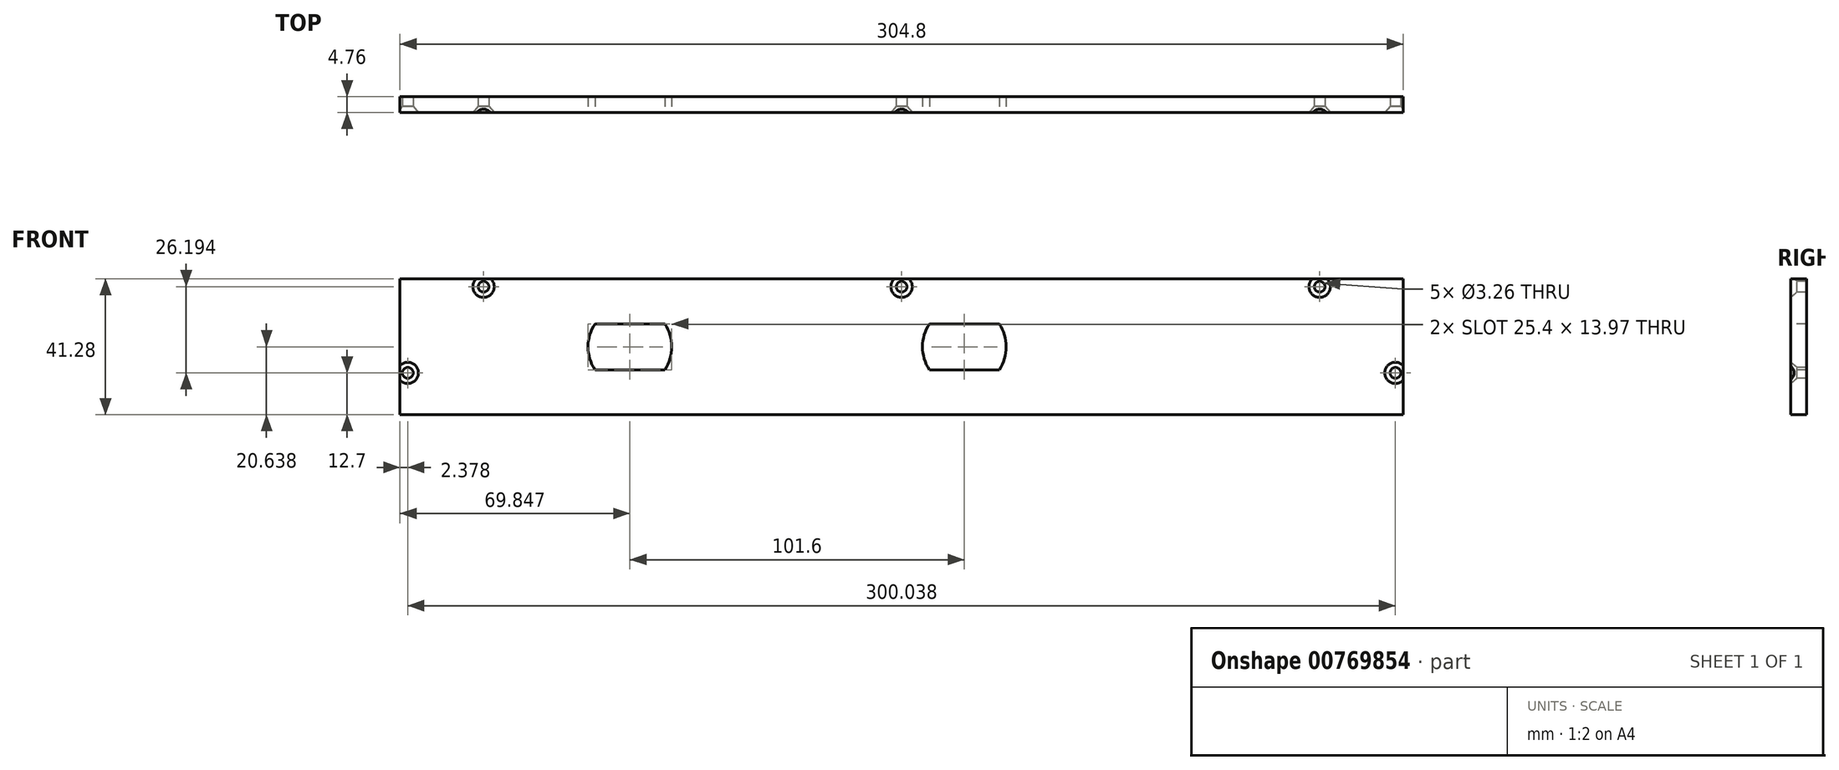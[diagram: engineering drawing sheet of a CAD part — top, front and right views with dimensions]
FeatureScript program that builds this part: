
annotation { "Feature Type Name" : "Feature", "Feature Type Description" : "" }
export const myFeature = defineFeature(function(context is Context, id is Id, definition is map)
    precondition{}
    {
        {
            var Q0;
            Q0=qCreatedBy(makeId("Front.planeOp"),FACE);
            var sketch = newSketch(context, id + "F0", { "sketchPlane" : qUnion([Q0])});
            skLineSegment(sketch, "E0.bottom", {"start": v(-119.12, 56.77) * mm, "end": v(185.68, 56.77) * mm});
            skLineSegment(sketch, "E0.top", {"start": v(-119.12, 15.5) * mm, "end": v(185.68, 15.5) * mm});
            skLineSegment(sketch, "E0.left", {"start": v(-119.12, 56.77) * mm, "end": v(-119.12, 15.5) * mm});
            skLineSegment(sketch, "E0.right", {"start": v(185.68, 56.77) * mm, "end": v(185.68, 15.5) * mm});
            skSolve(sketch);
        }
        {
            var Q0;
            Q0 = qSketchRegion(id + "F0", true);
            extrude(context, id + "F1", {"entities" : qUnion([Q0]), "depth" : 4.76 * mm, "offsetDistance" : 25.4 * mm});
        }
        {
            var Q0;
            Q0=makeQuery(id+"F1.opExtrude","CAP_FACE",FACE,{"disambiguationData":[OSD([sQuery(id+"F0.wireOp",EDGE,"E0.bottom"),sQuery(id+"F0.wireOp",EDGE,"E0.top"),sQuery(id+"F0.wireOp",EDGE,"E0.left"),sQuery(id+"F0.wireOp",EDGE,"E0.right")])],"isStart":false});
            var sketch = newSketch(context, id + "F2", { "sketchPlane" : qUnion([Q0])});
            skLineSegment(sketch, "E1", {"start": v(-116.74, 56.77) * mm, "end": v(-116.74, 15.5) * mm, "construction": true});
            skLineSegment(sketch, "E2", {"start": v(-119.12, 54.38) * mm, "end": v(185.68, 54.38) * mm, "construction": true});
            skLineSegment(sketch, "E3", {"start": v(183.3, 15.5) * mm, "end": v(183.3, 56.77) * mm, "construction": true});
            skPoint(sketch, "E4", {"position": v(-116.74, 28.2) * mm});
            skPoint(sketch, "E5", {"position": v(183.3, 28.2) * mm});
            skPoint(sketch, "E6", {"position": v(160.28, 54.38) * mm});
            skPoint(sketch, "E7", {"position": v(33.28, 54.38) * mm});
            skPoint(sketch, "E8", {"position": v(-93.72, 54.38) * mm});
            skSolve(sketch);
        }
        {
            var Q0;
            Q0=sQuery(id+"F2.wireOp",VERTEX,"E8");
            var Q1;
            Q1=sQuery(id+"F2.wireOp",VERTEX,"E4");
            var Q2;
            Q2=sQuery(id+"F2.wireOp",VERTEX,"E7");
            var Q3;
            Q3=sQuery(id+"F2.wireOp",VERTEX,"E6");
            var Q4;
            Q4=sQuery(id+"F2.wireOp",VERTEX,"E5");
            var Q5;
            Q5=makeQuery(id+"F1.opExtrude","SWEPT_BODY",BODY,{"disambiguationData":[OSD([sQuery(id+"F0.wireOp",EDGE,"E0.bottom"),sQuery(id+"F0.wireOp",EDGE,"E0.top"),sQuery(id+"F0.wireOp",EDGE,"E0.left"),sQuery(id+"F0.wireOp",EDGE,"E0.right")])]});
            hole(context, id + "F3", {"style" : HoleStyle.C_SINK, "endStyle" : HoleEndStyle.BLIND, "standardTappedOrClearance" : lookupTablePath({ "standard" : "ANSI", "fit" : "Normal (ASME)", "size" : "#4", "type" : "Clearance" }), "standardBlindInLast" : lookupTablePath({ "fit" : "Free", "standard" : "ANSI", "size" : "#4", "type" : "Clearance" }), "holeDiameter" : 3.26 * mm, "cSinkDiameter" : 6.48 * mm, "cSinkAngle" : 82 * degree, "majorDiameter" : 2.84 * mm, "holeDepth" : 14.6 * mm, "tappedDepth" : 12.7 * mm, "tapClearance" : 3, "locations" : qUnion([Q0, Q1, Q2, Q3, Q4]), "scope" : qUnion([Q5])});
        }
        {
            var Q0;
            Q0=makeQuery(id+"F1.opExtrude","CAP_FACE",FACE,{"disambiguationData":[OSD([sQuery(id+"F0.wireOp",EDGE,"E0.bottom"),sQuery(id+"F0.wireOp",EDGE,"E0.top"),sQuery(id+"F0.wireOp",EDGE,"E0.left"),sQuery(id+"F0.wireOp",EDGE,"E0.right")])],"isStart":false});
            var sketch = newSketch(context, id + "F4", { "sketchPlane" : qUnion([Q0])});
            skLineSegment(sketch, "E9", {"start": v(33.28, 15.5) * mm, "end": v(33.28, 56.77) * mm, "construction": true});
            skLineSegment(sketch, "E10", {"start": v(31.08, 56.77) * mm, "end": v(35.47, 56.77) * mm, "construction": true});
            skLineSegment(sketch, "E11", {"start": v(-119.12, 56.77) * mm, "end": v(-119.12, 15.5) * mm, "construction": true});
            skLineSegment(sketch, "E12", {"start": v(185.68, 56.77) * mm, "end": v(185.68, 15.5) * mm, "construction": true});
            skLineSegment(sketch, "E13", {"start": v(-119.12, 36.13) * mm, "end": v(185.68, 36.13) * mm, "construction": true});
            skArc(sketch, "E14", {"start": v(-59.88, 43.11) * mm, "mid": v(-61.97, 36.13) * mm, "end": v(-59.88, 29.14) * mm});
            skLineSegment(sketch, "E15.bottom", {"start": v(-59.88, 43.11) * mm, "end": v(-38.67, 43.11) * mm});
            skLineSegment(sketch, "E15.top", {"start": v(-59.88, 29.14) * mm, "end": v(-38.67, 29.14) * mm});
            skLineSegment(sketch, "E15.left", {"start": v(-59.88, 43.11) * mm, "end": v(-59.88, 29.14) * mm, "construction": true});
            skLineSegment(sketch, "E15.right", {"start": v(-38.67, 43.11) * mm, "end": v(-38.67, 29.14) * mm, "construction": true});
            skArc(sketch, "E16.trimOffspring", {"start": v(-38.67, 29.14) * mm, "mid": v(-36.57, 36.13) * mm, "end": v(-38.67, 43.11) * mm});
            skArc(sketch, "E17.MirrorCS", {"start": v(62.93, 43.11) * mm, "mid": v(65.03, 36.13) * mm, "end": v(62.93, 29.14) * mm});
            skLineSegment(sketch, "E18.MirrorCS", {"start": v(62.93, 43.11) * mm, "end": v(41.72, 43.11) * mm});
            skArc(sketch, "E19.MirrorCS", {"start": v(41.72, 29.14) * mm, "mid": v(39.63, 36.13) * mm, "end": v(41.72, 43.11) * mm});
            skLineSegment(sketch, "E20.MirrorCS", {"start": v(62.93, 29.14) * mm, "end": v(41.72, 29.14) * mm});
            skLineSegment(sketch, "E21", {"start": v(41.72, 43.11) * mm, "end": v(41.72, 29.14) * mm, "construction": true});
            skLineSegment(sketch, "E22", {"start": v(62.93, 43.11) * mm, "end": v(62.93, 29.14) * mm, "construction": true});
            skSolve(sketch);
        }
        {
            var Q0;
            Q0 = qSketchRegion(id + "F4", true);
            extrude(context, id + "F5", {"entities" : qUnion([Q0]), "operationType" : NewBodyOperationType.REMOVE, "oppositeDirection" : true, "depth" : 25.4 * mm, "offsetDistance" : 25.4 * mm});
        }
    });
